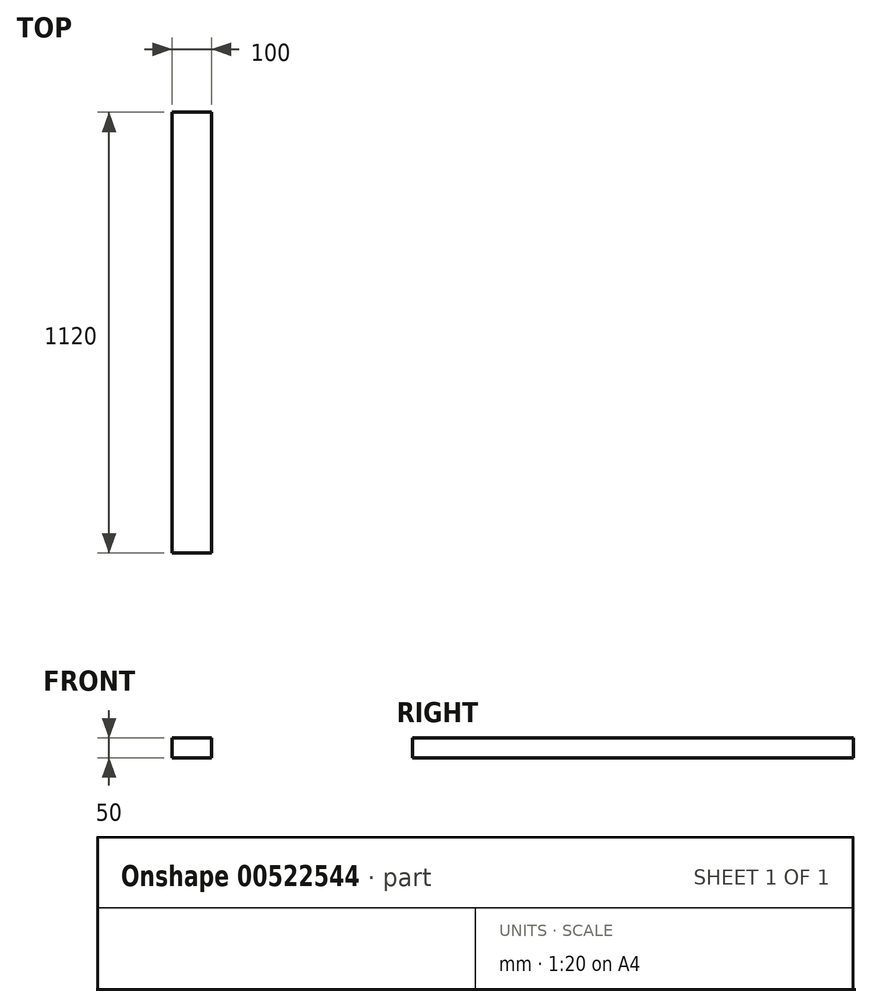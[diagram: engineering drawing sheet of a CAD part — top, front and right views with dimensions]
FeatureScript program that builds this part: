
annotation { "Feature Type Name" : "Feature", "Feature Type Description" : "" }
export const myFeature = defineFeature(function(context is Context, id is Id, definition is map)
    precondition{}
    {
        {
            var Q0;
            Q0=qCreatedBy(makeId("Front.planeOp"),FACE);
            var sketch = newSketch(context, id + "F0", { "sketchPlane" : qUnion([Q0])});
            skLineSegment(sketch, "E0.bottom", {"start": v(-139.39, 44.33) * mm, "end": v(-39.39, 44.33) * mm});
            skLineSegment(sketch, "E0.top", {"start": v(-139.39, -5.67) * mm, "end": v(-39.39, -5.67) * mm});
            skLineSegment(sketch, "E0.left", {"start": v(-139.39, 44.33) * mm, "end": v(-139.39, -5.67) * mm});
            skLineSegment(sketch, "E0.right", {"start": v(-39.39, 44.33) * mm, "end": v(-39.39, -5.67) * mm});
            skSolve(sketch);
        }
        {
            var Q0;
            Q0=qSketchRegion(id+"F0",true);
            extrude(context, id + "F1", {"entities" : qUnion([Q0]), "depth" : 1120 * mm, "offsetDistance" : 25 * mm});
        }
    });
